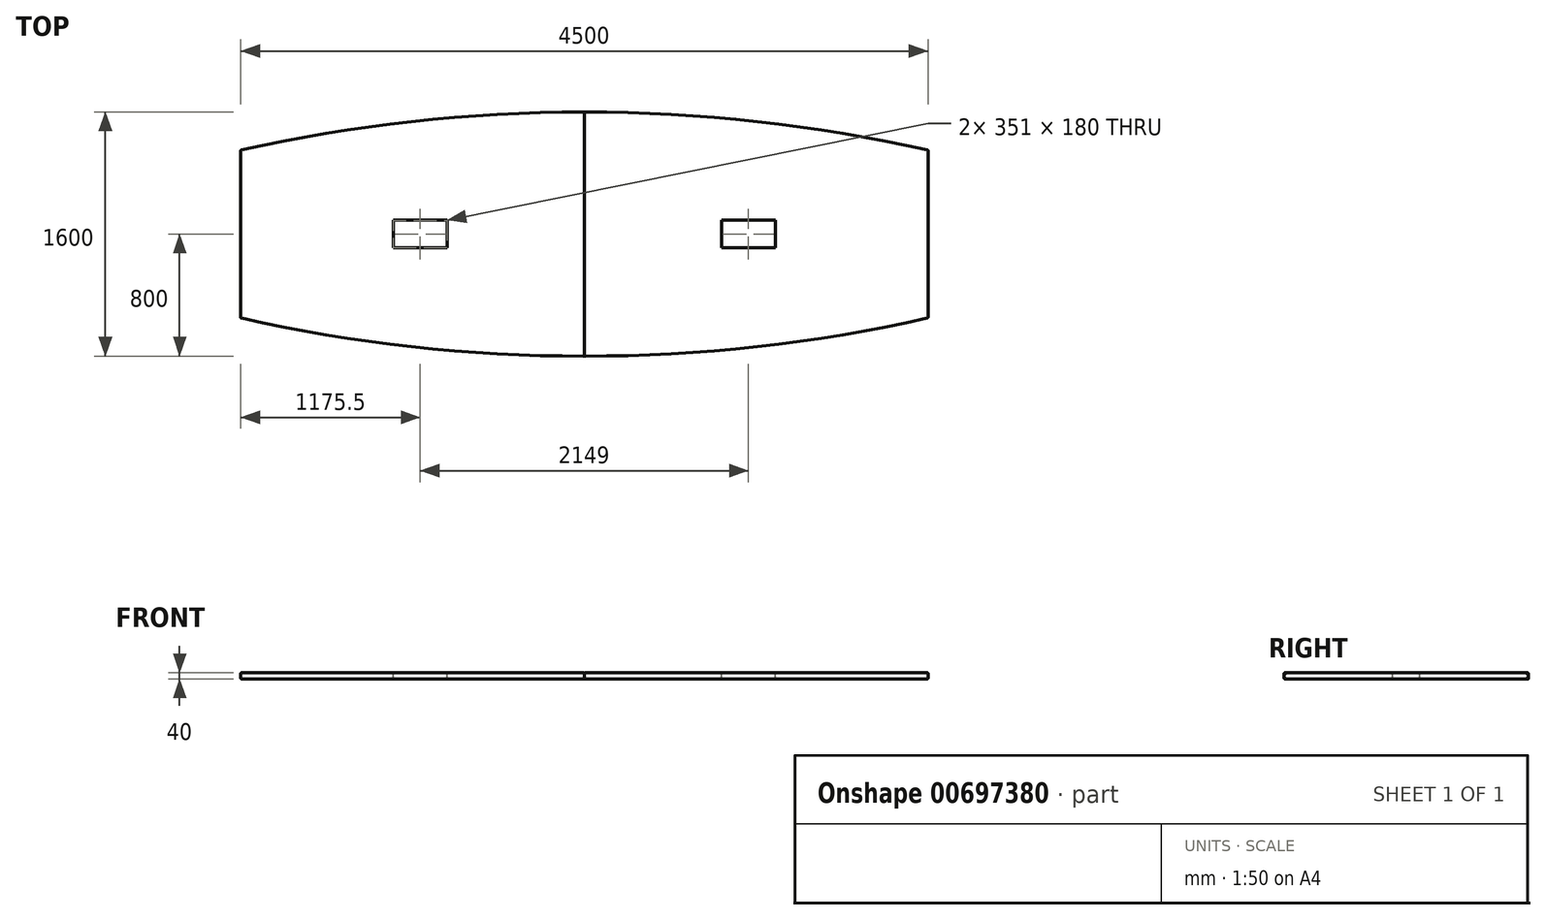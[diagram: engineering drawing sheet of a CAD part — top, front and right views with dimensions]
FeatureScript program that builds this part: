
annotation { "Feature Type Name" : "Feature", "Feature Type Description" : "" }
export const myFeature = defineFeature(function(context is Context, id is Id, definition is map)
    precondition{}
    {
        {
            var Q0;
            Q0=qCreatedBy(makeId("Top.planeOp"),FACE);
            var sketch = newSketch(context, id + "F0", { "sketchPlane" : qUnion([Q0])});
            skLineSegment(sketch, "E0.0", {"start": v(2250, -550) * mm, "end": v(2250, 550) * mm});
            skLineSegment(sketch, "E1.0", {"start": v(-2250, -550) * mm, "end": v(-2250, 550) * mm});
            skArc(sketch, "E2", {"start": v(2250, 550) * mm, "mid": v(0, 800) * mm, "end": v(-2250, 550) * mm});
            skArc(sketch, "E3", {"start": v(-2250, -550) * mm, "mid": v(0, -800) * mm, "end": v(2250, -550) * mm});
            skLineSegment(sketch, "E4", {"start": v(0, 800) * mm, "end": v(0, -800) * mm});
            skSolve(sketch);
        }
        {
            var Q0;
            Q0=makeQuery(id+"F0.imprint","IMPRINT",FACE,{"disambiguationData":[TD([[makeQuery(id+"F0.imprint","IMPRINT",EDGE,{"derivedFrom":sQuery(id+"F0.wireOp",EDGE,"E0.0")}),1.0]])]});
            extrude(context, id + "F1", {"entities" : qUnion([Q0]), "depth" : 40 * mm, "offsetDistance" : 25 * mm});
        }
        {
            var Q0;
            {var subQ0=sQuery(id+"F0.wireOp",EDGE,"E1.0");Q0=makeQuery(id+"F0.imprint","IMPRINT",FACE,{"disambiguationData":[TD([[makeQuery(id+"F0.imprint","IMPRINT",EDGE,{"derivedFrom":subQ0}),-1.0]])]});}
            extrude(context, id + "F2", {"entities" : qUnion([Q0]), "depth" : 40 * mm, "offsetDistance" : 25 * mm});
        }
        {
            var Q0;
            Q0=makeQuery(id+"F1.opExtrude","SWEPT_EDGE",EDGE,{"disambiguationData":[OSD([sQuery(id+"F0.wireOp",EDGE,"E0.0"),sQuery(id+"F0.wireOp",EDGE,"E3")])]});
            var Q1;
            Q1=makeQuery(id+"F1.opExtrude","SWEPT_EDGE",EDGE,{"disambiguationData":[OSD([sQuery(id+"F0.wireOp",EDGE,"E0.0"),sQuery(id+"F0.wireOp",EDGE,"E2")])]});
            var Q2;
            Q2=makeQuery(id+"F1.opExtrude","SWEPT_EDGE",EDGE,{"disambiguationData":[OSD([sQuery(id+"F0.wireOp",EDGE,"E3"),sQuery(id+"F0.wireOp",EDGE,"E4")])]});
            var Q3;
            Q3=makeQuery(id+"F1.opExtrude","SWEPT_EDGE",EDGE,{"disambiguationData":[OSD([sQuery(id+"F0.wireOp",EDGE,"E2"),sQuery(id+"F0.wireOp",EDGE,"E4")])]});
            var Q4;
            Q4=makeQuery(id+"F1.opExtrude","CAP_FACE",FACE,{"disambiguationData":[OSD([sQuery(id+"F0.wireOp",EDGE,"E0.0"),sQuery(id+"F0.wireOp",EDGE,"E2"),sQuery(id+"F0.wireOp",EDGE,"E3"),sQuery(id+"F0.wireOp",EDGE,"E4")])],"isStart":false});
            var Q5;
            Q5=makeQuery(id+"F1.opExtrude","CAP_FACE",FACE,{"disambiguationData":[OSD([sQuery(id+"F0.wireOp",EDGE,"E0.0"),sQuery(id+"F0.wireOp",EDGE,"E2"),sQuery(id+"F0.wireOp",EDGE,"E3"),sQuery(id+"F0.wireOp",EDGE,"E4")])],"isStart":true});
            fillet(context, id + "F3", {"entities" : qUnion([Q0, Q1, Q2, Q3, Q4, Q5]), "radius" : 5 * mm, "tangentPropagation" : true, "allowEdgeOverflow" : false});
        }
        {
            var Q0;
            Q0=makeQuery(id+"F2.opExtrude","SWEPT_EDGE",EDGE,{"disambiguationData":[OSD([sQuery(id+"F0.wireOp",EDGE,"E3"),sQuery(id+"F0.wireOp",EDGE,"E4")])]});
            var Q1;
            Q1=makeQuery(id+"F2.opExtrude","SWEPT_EDGE",EDGE,{"disambiguationData":[OSD([sQuery(id+"F0.wireOp",EDGE,"E1.0"),sQuery(id+"F0.wireOp",EDGE,"E3")])]});
            var Q2;
            Q2=makeQuery(id+"F2.opExtrude","SWEPT_EDGE",EDGE,{"disambiguationData":[OSD([sQuery(id+"F0.wireOp",EDGE,"E1.0"),sQuery(id+"F0.wireOp",EDGE,"E2")])]});
            var Q3;
            Q3=makeQuery(id+"F2.opExtrude","SWEPT_EDGE",EDGE,{"disambiguationData":[OSD([sQuery(id+"F0.wireOp",EDGE,"E2"),sQuery(id+"F0.wireOp",EDGE,"E4")])]});
            var Q4;
            Q4=makeQuery(id+"F2.opExtrude","CAP_FACE",FACE,{"disambiguationData":[OSD([sQuery(id+"F0.wireOp",EDGE,"E1.0"),sQuery(id+"F0.wireOp",EDGE,"E2"),sQuery(id+"F0.wireOp",EDGE,"E3"),sQuery(id+"F0.wireOp",EDGE,"E4")])],"isStart":false});
            var Q5;
            Q5=makeQuery(id+"F2.opExtrude","CAP_FACE",FACE,{"disambiguationData":[OSD([sQuery(id+"F0.wireOp",EDGE,"E1.0"),sQuery(id+"F0.wireOp",EDGE,"E2"),sQuery(id+"F0.wireOp",EDGE,"E3"),sQuery(id+"F0.wireOp",EDGE,"E4")])],"isStart":true});
            fillet(context, id + "F4", {"entities" : qUnion([Q0, Q1, Q2, Q3, Q4, Q5]), "radius" : 5 * mm, "tangentPropagation" : true, "allowEdgeOverflow" : false});
        }
        {
            var Q0;
            Q0=makeQuery(id+"F1.opExtrude","CAP_FACE",FACE,{"disambiguationData":[OSD([sQuery(id+"F0.wireOp",EDGE,"E0.0"),sQuery(id+"F0.wireOp",EDGE,"E2"),sQuery(id+"F0.wireOp",EDGE,"E3"),sQuery(id+"F0.wireOp",EDGE,"E4")])],"isStart":false});
            var sketch = newSketch(context, id + "F5", { "sketchPlane" : qUnion([Q0])});
            skLineSegment(sketch, "E5.bottom", {"start": v(899, 90) * mm, "end": v(1250, 90) * mm});
            skLineSegment(sketch, "E5.top", {"start": v(899, -90) * mm, "end": v(1250, -90) * mm});
            skLineSegment(sketch, "E5.left", {"start": v(899, 90) * mm, "end": v(899, -90) * mm});
            skLineSegment(sketch, "E5.right", {"start": v(1250, 90) * mm, "end": v(1250, -90) * mm});
            skSolve(sketch);
        }
        {
            var Q0;
            Q0=makeQuery(id+"F5.imprint","IMPRINT",FACE,{"disambiguationData":[TD([[makeQuery(id+"F5.imprint","IMPRINT",EDGE,{"derivedFrom":sQuery(id+"F5.wireOp",EDGE,"E5.bottom")}),-1.0]])]});
            extrude(context, id + "F6", {"entities" : qUnion([Q0]), "operationType" : NewBodyOperationType.REMOVE, "oppositeDirection" : true, "depth" : 40 * mm, "offsetDistance" : 25 * mm});
        }
        {
            var Q0;
            Q0=makeQuery(id+"F2.opExtrude","CAP_FACE",FACE,{"disambiguationData":[OSD([sQuery(id+"F0.wireOp",EDGE,"E1.0"),sQuery(id+"F0.wireOp",EDGE,"E2"),sQuery(id+"F0.wireOp",EDGE,"E3"),sQuery(id+"F0.wireOp",EDGE,"E4")])],"isStart":false});
            var sketch = newSketch(context, id + "F7", { "sketchPlane" : qUnion([Q0])});
            skLineSegment(sketch, "E6.bottom", {"start": v(-1250, 90) * mm, "end": v(-899, 90) * mm});
            skLineSegment(sketch, "E6.top", {"start": v(-1250, -90) * mm, "end": v(-899, -90) * mm});
            skLineSegment(sketch, "E6.left", {"start": v(-1250, 90) * mm, "end": v(-1250, -90) * mm});
            skLineSegment(sketch, "E6.right", {"start": v(-899, 90) * mm, "end": v(-899, -90) * mm});
            skSolve(sketch);
        }
        {
            var Q0;
            Q0=makeQuery(id+"F7.imprint","IMPRINT",FACE,{"disambiguationData":[TD([[makeQuery(id+"F7.imprint","IMPRINT",EDGE,{"derivedFrom":sQuery(id+"F7.wireOp",EDGE,"E6.bottom")}),-1.0]])]});
            extrude(context, id + "F8", {"entities" : qUnion([Q0]), "operationType" : NewBodyOperationType.REMOVE, "endBound" : BoundingType.THROUGH_ALL, "oppositeDirection" : true, "depth" : 25 * mm, "offsetDistance" : 25 * mm});
        }
    });
